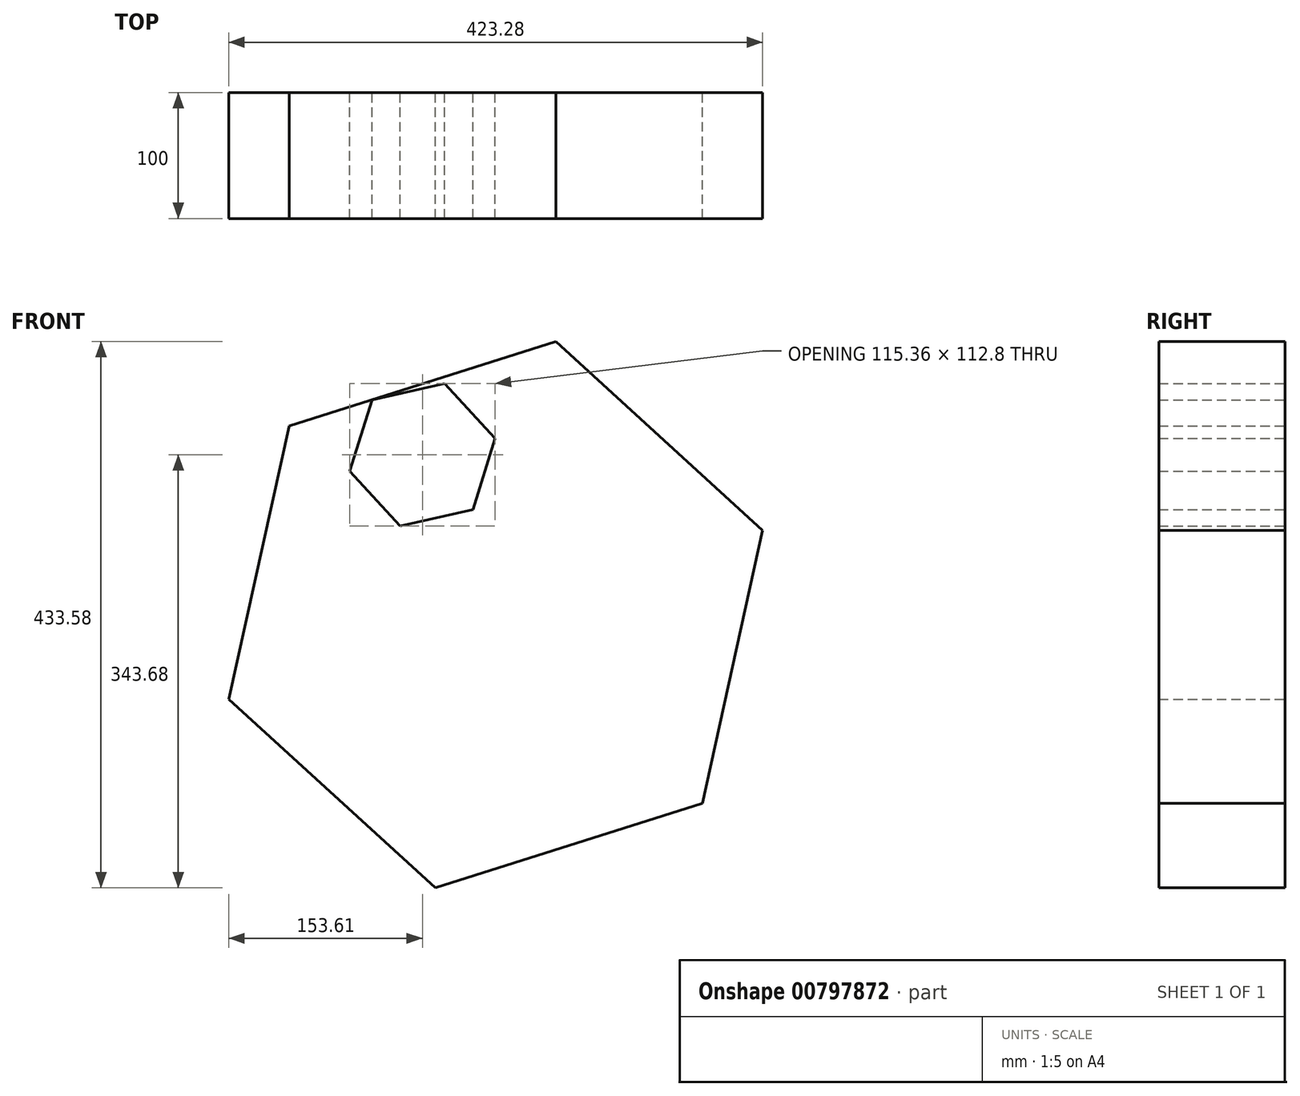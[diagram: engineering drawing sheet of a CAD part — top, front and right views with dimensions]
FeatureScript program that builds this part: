
annotation { "Feature Type Name" : "Feature", "Feature Type Description" : "" }
export const myFeature = defineFeature(function(context is Context, id is Id, definition is map)
    precondition{}
    {
        {
            var Q0;
            Q0=qCreatedBy(makeId("Front.planeOp"),FACE);
            var sketch = newSketch(context, id + "F0", { "sketchPlane" : qUnion([Q0])});
            skCircle(sketch, "E0.cCircle", {"center": v(0, 0) * mm, "radius": 51.18 * mm, "construction": true});
            skLineSegment(sketch, "E0.0", {"start": v(-17.67, -56.4) * mm, "end": v(-57.68, -12.9) * mm});
            skLineSegment(sketch, "E0.1", {"start": v(-57.68, -12.9) * mm, "end": v(-40, 43.5) * mm});
            skLineSegment(sketch, "E0.2", {"start": v(-40, 43.5) * mm, "end": v(17.67, 56.4) * mm});
            skLineSegment(sketch, "E0.3", {"start": v(17.67, 56.4) * mm, "end": v(57.68, 12.9) * mm});
            skLineSegment(sketch, "E0.4", {"start": v(57.68, 12.9) * mm, "end": v(40, -43.5) * mm});
            skLineSegment(sketch, "E0.5", {"start": v(40, -43.5) * mm, "end": v(-17.67, -56.4) * mm});
            skPoint(sketch, "E0.0.midPoint", {"position": v(-37.68, -34.65) * mm});
            skCircle(sketch, "E1.cCircle", {"center": v(58.03, -126.89) * mm, "radius": 192.25 * mm, "construction": true});
            skLineSegment(sketch, "E1.0", {"start": v(-105.82, 22.9) * mm, "end": v(105.82, 89.9) * mm});
            skLineSegment(sketch, "E1.1", {"start": v(105.82, 89.9) * mm, "end": v(269.67, -59.88) * mm});
            skLineSegment(sketch, "E1.2", {"start": v(269.67, -59.88) * mm, "end": v(221.88, -276.67) * mm});
            skLineSegment(sketch, "E1.3", {"start": v(221.88, -276.67) * mm, "end": v(10.24, -343.68) * mm});
            skLineSegment(sketch, "E1.4", {"start": v(10.24, -343.68) * mm, "end": v(-153.61, -193.9) * mm});
            skLineSegment(sketch, "E1.5", {"start": v(-153.61, -193.9) * mm, "end": v(-105.82, 22.9) * mm});
            skPoint(sketch, "E1.0.midPoint", {"position": v(0, 56.4) * mm});
            skSolve(sketch);
        }
        {
            var Q0;
            Q0 = qSketchRegion(id + "F0", true);
            extrude(context, id + "F1", {"entities" : qUnion([Q0]), "depth" : 100 * mm, "offsetDistance" : 25.4 * mm});
        }
    });
